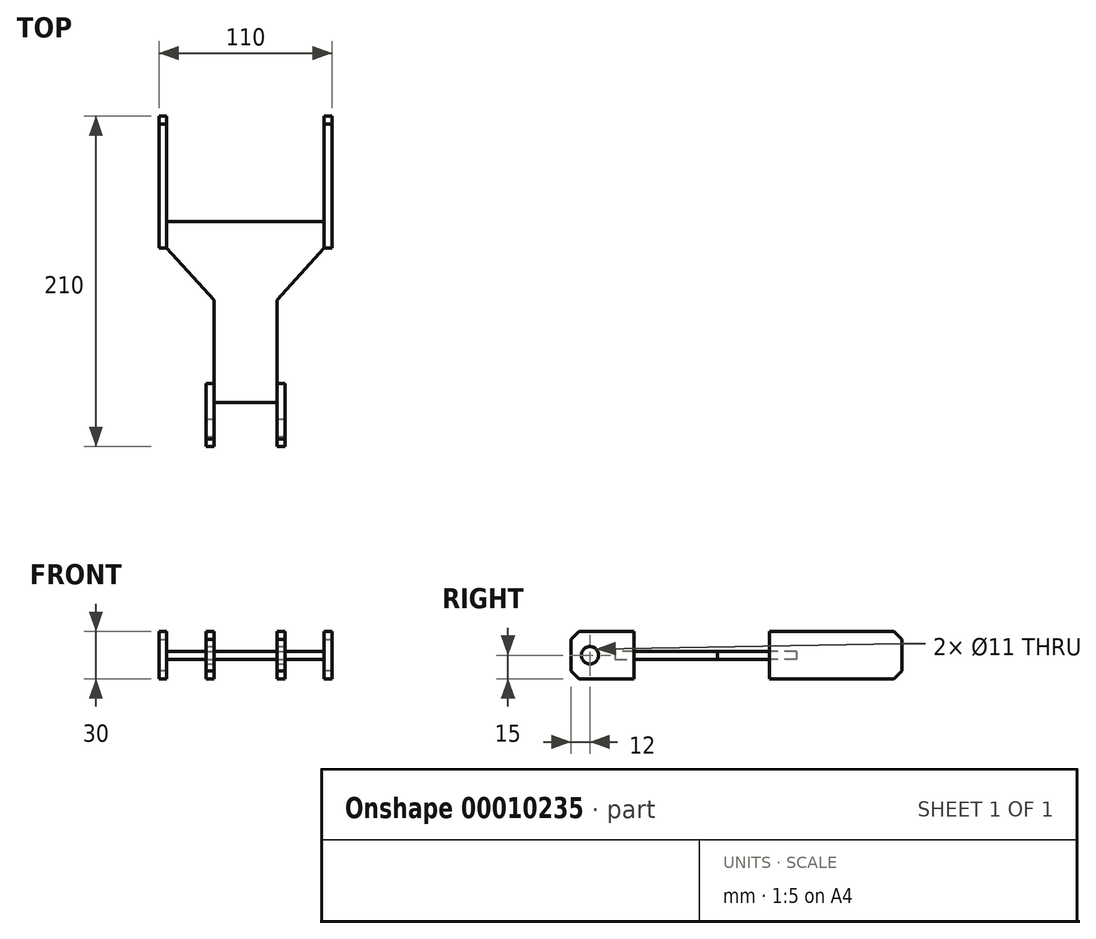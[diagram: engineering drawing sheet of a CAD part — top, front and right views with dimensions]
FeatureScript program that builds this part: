
annotation { "Feature Type Name" : "Feature", "Feature Type Description" : "" }
export const myFeature = defineFeature(function(context is Context, id is Id, definition is map)
    precondition{}
    {
        {
            var Q0;
            Q0=qCreatedBy(makeId("Front.planeOp"),FACE);
            var sketch = newSketch(context, id + "F0", { "sketchPlane" : qUnion([Q0])});
            skLineSegment(sketch, "E0.bottom", {"start": v(-20, 2.5) * mm, "end": v(20, 2.5) * mm});
            skLineSegment(sketch, "E0.top", {"start": v(-20, -2.5) * mm, "end": v(20, -2.5) * mm});
            skLineSegment(sketch, "E0.left", {"start": v(-20, 2.5) * mm, "end": v(-20, -2.5) * mm});
            skLineSegment(sketch, "E0.right", {"start": v(20, 2.5) * mm, "end": v(20, -2.5) * mm});
            skSolve(sketch);
        }
        {
            var Q0;
            Q0=makeQuery(id+"F0.imprint","IMPRINT",FACE,{"disambiguationData":[TD([[makeQuery(id+"F0.imprint","IMPRINT",EDGE,{"derivedFrom":sQuery(id+"F0.wireOp",EDGE,"E0.bottom")}),-1.0]])]});
            extrude(context, id + "F1", {"entities" : qUnion([Q0]), "oppositeDirection" : true, "depth" : 65 * mm});
        }
        {
            var Q0;
            Q0=qCreatedBy(makeId("Top.planeOp"),FACE);
            var sketch = newSketch(context, id + "F2", { "sketchPlane" : qUnion([Q0])});
            skLineSegment(sketch, "E1", {"start": v(-20, 65) * mm, "end": v(20, 65) * mm});
            skLineSegment(sketch, "E2", {"start": v(20, 65) * mm, "end": v(50, 98) * mm});
            skLineSegment(sketch, "E3", {"start": v(50, 98) * mm, "end": v(-50, 98) * mm});
            skLineSegment(sketch, "E4", {"start": v(-50, 98) * mm, "end": v(-20, 65) * mm});
            skSolve(sketch);
        }
        {
            var Q0;
            Q0=makeQuery(id+"F2.imprint","IMPRINT",FACE,{"disambiguationData":[TD([[makeQuery(id+"F2.imprint","IMPRINT",EDGE,{"derivedFrom":sQuery(id+"F2.wireOp",EDGE,"E1")}),1.0]])]});
            extrude(context, id + "F3", {"entities" : qUnion([Q0]), "operationType" : NewBodyOperationType.ADD, "endBound" : BoundingType.SYMMETRIC, "depth" : 5 * mm});
        }
        {
            var Q0;
            Q0=makeQuery(id+"F3.opExtrude","SWEPT_FACE",FACE,{"disambiguationData":[OSD([sQuery(id+"F2.wireOp",EDGE,"E3")])]});
            extrude(context, id + "F4", {"entities" : qUnion([Q0]), "operationType" : NewBodyOperationType.ADD, "depth" : 17 * mm});
        }
        {
            var Q0;
            Q0=makeQuery(id+"F4.opExtrude","SWEPT_FACE",FACE,{"disambiguationData":[OSD([sQuery(id+"F2.wireOp",EDGE,"E2"),sQuery(id+"F2.wireOp",EDGE,"E3")])]});
            var sketch = newSketch(context, id + "F5", { "sketchPlane" : qUnion([Q0])});
            skLineSegment(sketch, "E5.bottom", {"start": v(98, 15) * mm, "end": v(182, 15) * mm});
            skLineSegment(sketch, "E5.top", {"start": v(98, -15) * mm, "end": v(182, -15) * mm});
            skLineSegment(sketch, "E5.left", {"start": v(98, 15) * mm, "end": v(98, -15) * mm});
            skLineSegment(sketch, "E5.right", {"start": v(182, 15) * mm, "end": v(182, -15) * mm});
            skSolve(sketch);
        }
        {
            var Q0;
            {var subQ6=sQuery(id+"F5.wireOp",EDGE,"E5.bottom");Q0=makeQuery(id+"F5.imprint","IMPRINT",FACE,{"disambiguationData":[TD([[makeQuery(id+"F5.imprint","IMPRINT",EDGE,{"derivedFrom":subQ6}),-1.0]])]});}
            var Q1;
            {var subQ0=sQuery(id+"F2.wireOp",EDGE,"E2");var subQ1=sQuery(id+"F2.wireOp",EDGE,"E3");Q1=makeQuery(id+"F5.imprint","IMPRINT",FACE,{"disambiguationData":[TD([[makeQuery(id+"F5.imprint","IMPRINT",EDGE,{"derivedFrom":makeQuery(id+"F4.opExtrude","CAP_EDGE",EDGE,{"disambiguationData":[OSD([subQ0,subQ1])],"isStart":false})}),-1.0]])]});}
            extrude(context, id + "F6", {"entities" : qUnion([Q0, Q1]), "depth" : 5 * mm});
        }
        {
            var Q0;
            Q0=makeQuery(id+"F6.opExtrude","SWEPT_BODY",BODY,{"disambiguationData":[OSD([sQuery(id+"F5.wireOp",EDGE,"E5.bottom"),sQuery(id+"F5.wireOp",EDGE,"E5.top"),sQuery(id+"F5.wireOp",EDGE,"E5.left"),sQuery(id+"F5.wireOp",EDGE,"E5.right")])]});
            var Q1;
            Q1=qCreatedBy(makeId("Right.planeOp"),FACE);
            mirror(context, id + "F7", {"entities" : qUnion([Q0]), "mirrorPlane" : qUnion([Q1])});
        }
        {
            var Q0;
            Q0=makeQuery(id+"F1.opExtrude","SWEPT_FACE",FACE,{"disambiguationData":[OSD([sQuery(id+"F0.wireOp",EDGE,"E0.left")])]});
            var sketch = newSketch(context, id + "F8", { "sketchPlane" : qUnion([Q0])});
            skLineSegment(sketch, "E6.bottom", {"start": v(-12, 15) * mm, "end": v(28, 15) * mm});
            skLineSegment(sketch, "E6.top", {"start": v(-12, -15) * mm, "end": v(28, -15) * mm});
            skLineSegment(sketch, "E6.left", {"start": v(-12, 15) * mm, "end": v(-12, -15) * mm});
            skLineSegment(sketch, "E6.right", {"start": v(28, 15) * mm, "end": v(28, -15) * mm});
            skSolve(sketch);
        }
        {
            var Q0;
            {var subQ8=sQuery(id+"F8.wireOp",EDGE,"E6.bottom");Q0=makeQuery(id+"F8.imprint","IMPRINT",FACE,{"disambiguationData":[TD([[makeQuery(id+"F8.imprint","IMPRINT",EDGE,{"derivedFrom":subQ8}),-1.0]])]});}
            var Q1;
            {var subQ0=sQuery(id+"F0.wireOp",EDGE,"E0.left");var subQ4=makeQuery(id+"F1.opExtrude","CAP_EDGE",EDGE,{"disambiguationData":[OSD([subQ0])],"isStart":true});Q1=makeQuery(id+"F8.imprint","IMPRINT",FACE,{"disambiguationData":[TD([[makeQuery(id+"F8.imprint","IMPRINT",EDGE,{"derivedFrom":subQ4}),-1.0]])]});}
            extrude(context, id + "F9", {"entities" : qUnion([Q0, Q1]), "operationType" : NewBodyOperationType.ADD, "depth" : 5 * mm});
        }
        {
            var Q0;
            Q0=makeQuery(id+"F1.opExtrude","SWEPT_FACE",FACE,{"disambiguationData":[OSD([sQuery(id+"F0.wireOp",EDGE,"E0.right")])]});
            var sketch = newSketch(context, id + "F10", { "sketchPlane" : qUnion([Q0])});
            skLineSegment(sketch, "E7.bottom", {"start": v(-28, 15) * mm, "end": v(12, 15) * mm});
            skLineSegment(sketch, "E7.top", {"start": v(-28, -15) * mm, "end": v(12, -15) * mm});
            skLineSegment(sketch, "E7.left", {"start": v(-28, 15) * mm, "end": v(-28, -15) * mm});
            skLineSegment(sketch, "E7.right", {"start": v(12, 15) * mm, "end": v(12, -15) * mm});
            skSolve(sketch);
        }
        {
            var Q0;
            {var subQ8=sQuery(id+"F10.wireOp",EDGE,"E7.bottom");Q0=makeQuery(id+"F10.imprint","IMPRINT",FACE,{"disambiguationData":[TD([[makeQuery(id+"F10.imprint","IMPRINT",EDGE,{"derivedFrom":subQ8}),-1.0]])]});}
            var Q1;
            {var subQ0=sQuery(id+"F0.wireOp",EDGE,"E0.right");var subQ4=makeQuery(id+"F1.opExtrude","CAP_EDGE",EDGE,{"disambiguationData":[OSD([subQ0])],"isStart":true});Q1=makeQuery(id+"F10.imprint","IMPRINT",FACE,{"disambiguationData":[TD([[makeQuery(id+"F10.imprint","IMPRINT",EDGE,{"derivedFrom":subQ4}),1.0]])]});}
            extrude(context, id + "F11", {"entities" : qUnion([Q0, Q1]), "operationType" : NewBodyOperationType.ADD, "depth" : 5 * mm});
        }
        {
            var Q0;
            Q0=makeQuery(id+"F6.opExtrude","CAP_FACE",FACE,{"disambiguationData":[OSD([sQuery(id+"F5.wireOp",EDGE,"E5.bottom"),sQuery(id+"F5.wireOp",EDGE,"E5.top"),sQuery(id+"F5.wireOp",EDGE,"E5.left"),sQuery(id+"F5.wireOp",EDGE,"E5.right")])],"isStart":false});
            var sketch = newSketch(context, id + "F12", { "sketchPlane" : qUnion([Q0])});
            skPoint(sketch, "E8", {"position": v(-16, 0) * mm});
            skPoint(sketch, "E9", {"position": v(259.76, 0) * mm});
            skPoint(sketch, "E10", {"position": v(170, 0) * mm});
            skSolve(sketch);
        }
        {
            var Q0;
            Q0=sQuery(id+"F12.wireOp",VERTEX,"E8");
            var Q1;
            Q1=sQuery(id+"F12.wireOp",VERTEX,"E10");
            var Q2;
            Q2=makeQuery(id+"F1.opExtrude","SWEPT_BODY",BODY,{"disambiguationData":[OSD([sQuery(id+"F0.wireOp",EDGE,"E0.bottom"),sQuery(id+"F0.wireOp",EDGE,"E0.top"),sQuery(id+"F0.wireOp",EDGE,"E0.left"),sQuery(id+"F0.wireOp",EDGE,"E0.right")])]});
            hole(context, id + "F13", {"style" : HoleStyle.SIMPLE, "holeDiameter" : 11 * mm, "endStyle" : HoleEndStyle.THROUGH, "locations" : qUnion([Q0, Q1]), "scope" : qUnion([Q2])});
        }
        {
            var Q0;
            Q0=makeQuery(id+"F9.opExtrude","SWEPT_EDGE",EDGE,{"disambiguationData":[OSD([sQuery(id+"F8.wireOp",EDGE,"E6.bottom"),sQuery(id+"F8.wireOp",EDGE,"E6.right")])]});
            var Q1;
            Q1=makeQuery(id+"F11.opExtrude","SWEPT_EDGE",EDGE,{"disambiguationData":[OSD([sQuery(id+"F10.wireOp",EDGE,"E7.bottom"),sQuery(id+"F10.wireOp",EDGE,"E7.left")])]});
            var Q2;
            Q2=makeQuery(id+"F9.opExtrude","SWEPT_EDGE",EDGE,{"disambiguationData":[OSD([sQuery(id+"F8.wireOp",EDGE,"E6.top"),sQuery(id+"F8.wireOp",EDGE,"E6.right")])]});
            var Q3;
            Q3=makeQuery(id+"F11.opExtrude","SWEPT_EDGE",EDGE,{"disambiguationData":[OSD([sQuery(id+"F10.wireOp",EDGE,"E7.top"),sQuery(id+"F10.wireOp",EDGE,"E7.left")])]});
            chamfer(context, id + "F14", {"entities" : qUnion([Q0, Q1, Q2, Q3]), "width" : 5 * mm, "tangentPropagation" : true});
        }
        {
            var Q0;
            Q0=makeQuery(id+"F6.opExtrude","SWEPT_EDGE",EDGE,{"disambiguationData":[OSD([sQuery(id+"F5.wireOp",EDGE,"E5.bottom"),sQuery(id+"F5.wireOp",EDGE,"E5.right")])]});
            var Q1;
            Q1=makeQuery(id+"F6.opExtrude","SWEPT_EDGE",EDGE,{"disambiguationData":[OSD([sQuery(id+"F5.wireOp",EDGE,"E5.top"),sQuery(id+"F5.wireOp",EDGE,"E5.right")])]});
            var Q2;
            Q2=makeQuery(id+"F7.opPattern","COPY",EDGE,{"derivedFrom":makeQuery(id+"F6.opExtrude","SWEPT_EDGE",EDGE,{"disambiguationData":[OSD([sQuery(id+"F5.wireOp",EDGE,"E5.top"),sQuery(id+"F5.wireOp",EDGE,"E5.right")])]}),"instanceName":"1"});
            var Q3;
            Q3=makeQuery(id+"F7.opPattern","COPY",EDGE,{"derivedFrom":makeQuery(id+"F6.opExtrude","SWEPT_EDGE",EDGE,{"disambiguationData":[OSD([sQuery(id+"F5.wireOp",EDGE,"E5.bottom"),sQuery(id+"F5.wireOp",EDGE,"E5.right")])]}),"instanceName":"1"});
            chamfer(context, id + "F15", {"entities" : qUnion([Q0, Q1, Q2, Q3]), "width" : 5 * mm, "tangentPropagation" : true});
        }
    });
